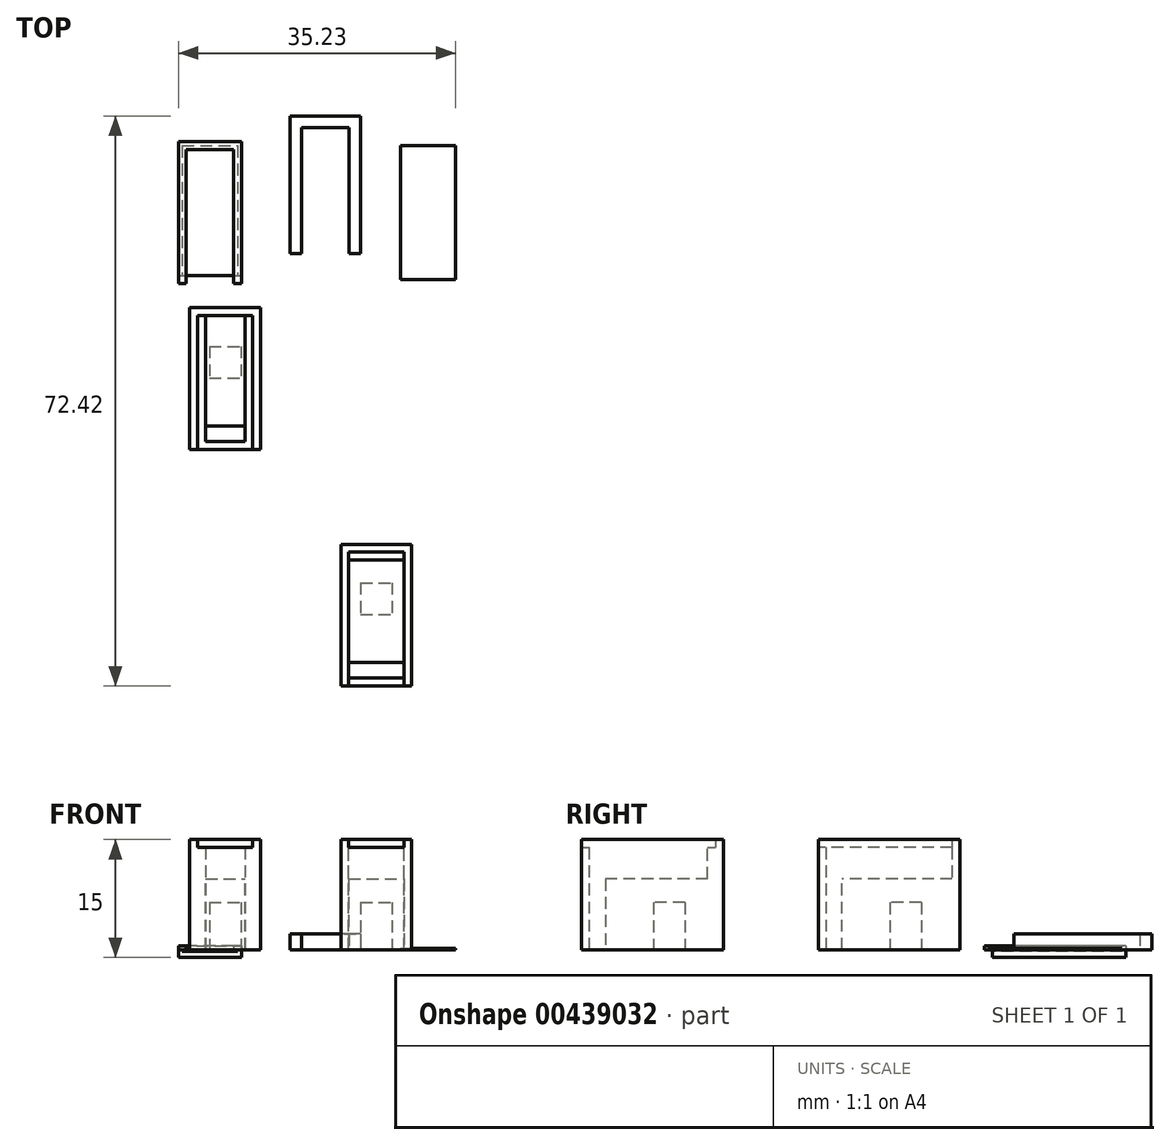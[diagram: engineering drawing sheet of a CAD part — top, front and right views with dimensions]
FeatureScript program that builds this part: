
annotation { "Feature Type Name" : "Feature", "Feature Type Description" : "" }
export const myFeature = defineFeature(function(context is Context, id is Id, definition is map)
    precondition{}
    {
        {
            var Q0;
            Q0=qCreatedBy(makeId("Top.planeOp"),FACE);
            var sketch = newSketch(context, id + "F0", { "sketchPlane" : qUnion([Q0])});
            skLineSegment(sketch, "E0.bottom", {"start": v(4.5, -9) * mm, "end": v(-4.5, -9) * mm});
            skLineSegment(sketch, "E0.top", {"start": v(4.5, 9) * mm, "end": v(-4.5, 9) * mm});
            skLineSegment(sketch, "E0.left", {"start": v(4.5, -9) * mm, "end": v(4.5, 9) * mm});
            skLineSegment(sketch, "E0.right", {"start": v(-4.5, -9) * mm, "end": v(-4.5, 9) * mm});
            skPoint(sketch, "E0.middle", {"position": v(0, 0) * mm});
            skSolve(sketch);
        }
        {
            var Q0;
            Q0=qSketchRegion(id+"F0",true);
            extrude(context, id + "F1", {"entities" : qUnion([Q0]), "depth" : 13 * mm});
        }
        {
            var Q0;
            Q0=makeQuery(id+"F1.opExtrude","CAP_FACE",FACE,{"disambiguationData":[OSD([sQuery(id+"F0.wireOp",EDGE,"E0.bottom"),sQuery(id+"F0.wireOp",EDGE,"E0.top"),sQuery(id+"F0.wireOp",EDGE,"E0.left"),sQuery(id+"F0.wireOp",EDGE,"E0.right")])],"isStart":true});
            var sketch = newSketch(context, id + "F2", { "sketchPlane" : qUnion([Q0])});
            skLineSegment(sketch, "E1.bottom", {"start": v(-2, -4.1) * mm, "end": v(2, -4.1) * mm});
            skLineSegment(sketch, "E1.top", {"start": v(-2, -0.1) * mm, "end": v(2, -0.1) * mm});
            skLineSegment(sketch, "E1.left", {"start": v(-2, -4.1) * mm, "end": v(-2, -0.1) * mm});
            skLineSegment(sketch, "E1.right", {"start": v(2, -4.1) * mm, "end": v(2, -0.1) * mm});
            skPoint(sketch, "E1.middle", {"position": v(0, -2.1) * mm});
            skSolve(sketch);
        }
        {
            var Q0;
            Q0=qSketchRegion(id+"F2",true);
            extrude(context, id + "F3", {"entities" : qUnion([Q0]), "operationType" : NewBodyOperationType.REMOVE, "oppositeDirection" : true, "depth" : 6 * mm});
        }
        {
            var Q0;
            Q0=makeQuery(id+"F1.opExtrude","SWEPT_FACE",FACE,{"disambiguationData":[OSD([sQuery(id+"F0.wireOp",EDGE,"E0.bottom")])]});
            var sketch = newSketch(context, id + "F4", { "sketchPlane" : qUnion([Q0])});
            skLineSegment(sketch, "E2.bottom", {"start": v(-2.5, 13) * mm, "end": v(2.5, 13) * mm});
            skLineSegment(sketch, "E2.top", {"start": v(-2.5, 9) * mm, "end": v(2.5, 9) * mm});
            skLineSegment(sketch, "E2.left", {"start": v(-2.5, 13) * mm, "end": v(-2.5, 9) * mm});
            skLineSegment(sketch, "E2.right", {"start": v(2.5, 13) * mm, "end": v(2.5, 9) * mm});
            skSolve(sketch);
        }
        {
            var Q0;
            Q0=qSketchRegion(id+"F4",true);
            extrude(context, id + "F5", {"entities" : qUnion([Q0]), "operationType" : NewBodyOperationType.REMOVE, "oppositeDirection" : true, "depth" : 17 * mm});
        }
        {
            var Q0;
            Q0=qCreatedBy(makeId("Top.planeOp"),FACE);
            var sketch = newSketch(context, id + "F6", { "sketchPlane" : qUnion([Q0])});
            skLineSegment(sketch, "E3", {"start": v(-5.95, 12.1) * mm, "end": v(-5.95, 30.1) * mm});
            skLineSegment(sketch, "E4", {"start": v(-5.95, 30.1) * mm, "end": v(2.05, 30.1) * mm});
            skLineSegment(sketch, "E5", {"start": v(2.05, 30.1) * mm, "end": v(2.05, 12.1) * mm});
            skLineSegment(sketch, "E6", {"start": v(2.05, 12.1) * mm, "end": v(1.05, 12.1) * mm});
            skLineSegment(sketch, "E7", {"start": v(1.05, 12.1) * mm, "end": v(1.05, 29.1) * mm});
            skLineSegment(sketch, "E8", {"start": v(1.05, 29.1) * mm, "end": v(-4.95, 29.1) * mm});
            skLineSegment(sketch, "E9", {"start": v(-4.95, 29.1) * mm, "end": v(-4.95, 12.1) * mm});
            skLineSegment(sketch, "E10", {"start": v(-4.95, 12.1) * mm, "end": v(-5.95, 12.1) * mm});
            skSolve(sketch);
        }
        {
            var Q0;
            Q0=qSketchRegion(id+"F6",true);
            extrude(context, id + "F7", {"entities" : qUnion([Q0]), "depth" : 0.5 * mm});
        }
        {
            var Q0;
            Q0=qCreatedBy(makeId("Top.planeOp"),FACE);
            var sketch = newSketch(context, id + "F8", { "sketchPlane" : qUnion([Q0])});
            skLineSegment(sketch, "E11.bottom", {"start": v(-5.95, 13.1) * mm, "end": v(2.05, 13.1) * mm});
            skLineSegment(sketch, "E11.top", {"start": v(-5.95, 30.1) * mm, "end": v(2.05, 30.1) * mm});
            skLineSegment(sketch, "E11.left", {"start": v(-5.95, 13.1) * mm, "end": v(-5.95, 30.1) * mm});
            skLineSegment(sketch, "E11.right", {"start": v(2.05, 13.1) * mm, "end": v(2.05, 30.1) * mm});
            skSolve(sketch);
        }
        {
            var Q0;
            Q0=qSketchRegion(id+"F8",true);
            extrude(context, id + "F9", {"entities" : qUnion([Q0]), "oppositeDirection" : true, "depth" : 1 * mm});
        }
        {
            var Q0;
            Q0=makeQuery(id+"F9.opExtrude","SWEPT_FACE",FACE,{"disambiguationData":[OSD([sQuery(id+"F8.wireOp",EDGE,"E11.bottom")])]});
            var sketch = newSketch(context, id + "F10", { "sketchPlane" : qUnion([Q0])});
            skLineSegment(sketch, "E12.bottom", {"start": v(-5.45, 0) * mm, "end": v(1.55, 0) * mm});
            skLineSegment(sketch, "E12.top", {"start": v(-5.45, -0.2) * mm, "end": v(1.55, -0.2) * mm});
            skLineSegment(sketch, "E12.left", {"start": v(-5.45, 0) * mm, "end": v(-5.45, -0.2) * mm});
            skLineSegment(sketch, "E12.right", {"start": v(1.55, 0) * mm, "end": v(1.55, -0.2) * mm});
            skSolve(sketch);
        }
        {
            var Q0;
            Q0=qSketchRegion(id+"F10",true);
            extrude(context, id + "F11", {"entities" : qUnion([Q0]), "operationType" : NewBodyOperationType.REMOVE, "oppositeDirection" : true, "depth" : 16.5 * mm});
        }
        {
            var Q0;
            Q0=qCreatedBy(makeId("Top.planeOp"),FACE);
            var sketch = newSketch(context, id + "F12", { "sketchPlane" : qUnion([Q0])});
            skLineSegment(sketch, "E13", {"start": v(8.22, 15.87) * mm, "end": v(8.22, 33.37) * mm});
            skLineSegment(sketch, "E14", {"start": v(8.22, 33.37) * mm, "end": v(17.22, 33.37) * mm});
            skLineSegment(sketch, "E15", {"start": v(17.22, 33.37) * mm, "end": v(17.22, 15.87) * mm});
            skLineSegment(sketch, "E16", {"start": v(17.22, 15.87) * mm, "end": v(15.72, 15.87) * mm});
            skLineSegment(sketch, "E17", {"start": v(15.72, 15.87) * mm, "end": v(15.72, 31.87) * mm});
            skLineSegment(sketch, "E18", {"start": v(15.72, 31.87) * mm, "end": v(9.72, 31.87) * mm});
            skLineSegment(sketch, "E19", {"start": v(9.72, 31.87) * mm, "end": v(9.72, 15.87) * mm});
            skLineSegment(sketch, "E20", {"start": v(9.72, 15.87) * mm, "end": v(8.22, 15.87) * mm});
            skSolve(sketch);
        }
        {
            var Q0;
            Q0=qSketchRegion(id+"F12",true);
            extrude(context, id + "F13", {"entities" : qUnion([Q0]), "depth" : 2 * mm});
        }
        {
            var Q0;
            Q0=qCreatedBy(makeId("Top.planeOp"),FACE);
            var sketch = newSketch(context, id + "F14", { "sketchPlane" : qUnion([Q0])});
            skLineSegment(sketch, "E21.bottom", {"start": v(22.28, 12.58) * mm, "end": v(29.28, 12.58) * mm});
            skLineSegment(sketch, "E21.top", {"start": v(22.28, 29.58) * mm, "end": v(29.28, 29.58) * mm});
            skLineSegment(sketch, "E21.left", {"start": v(22.28, 12.58) * mm, "end": v(22.28, 29.58) * mm});
            skLineSegment(sketch, "E21.right", {"start": v(29.28, 12.58) * mm, "end": v(29.28, 29.58) * mm});
            skSolve(sketch);
        }
        {
            var Q0;
            Q0=qSketchRegion(id+"F14",true);
            extrude(context, id + "F15", {"entities" : qUnion([Q0]), "depth" : 0.2 * mm});
        }
        {
            var Q0;
            Q0=makeQuery(id+"F5.boolean.opBoolean","COPY",FACE,{"derivedFrom":makeQuery(id+"F5.opExtrude","SWEPT_FACE",FACE,{"disambiguationData":[OSD([sQuery(id+"F4.wireOp",EDGE,"E2.top")])]})});
            var sketch = newSketch(context, id + "F16", { "sketchPlane" : qUnion([Q0])});
            skLineSegment(sketch, "E22.bottom", {"start": v(-2.5, -9) * mm, "end": v(2.5, -9) * mm});
            skLineSegment(sketch, "E22.top", {"start": v(-2.5, -6) * mm, "end": v(2.5, -6) * mm});
            skLineSegment(sketch, "E22.left", {"start": v(-2.5, -9) * mm, "end": v(-2.5, -6) * mm});
            skLineSegment(sketch, "E22.right", {"start": v(2.5, -9) * mm, "end": v(2.5, -6) * mm});
            skSolve(sketch);
        }
        {
            var Q0;
            Q0=qSketchRegion(id+"F16",true);
            extrude(context, id + "F17", {"entities" : qUnion([Q0]), "operationType" : NewBodyOperationType.REMOVE, "oppositeDirection" : true, "depth" : 25 * mm});
        }
        {
            var Q0;
            Q0=makeQuery(id+"F1.opExtrude","CAP_FACE",FACE,{"disambiguationData":[OSD([sQuery(id+"F0.wireOp",EDGE,"E0.bottom"),sQuery(id+"F0.wireOp",EDGE,"E0.top"),sQuery(id+"F0.wireOp",EDGE,"E0.left"),sQuery(id+"F0.wireOp",EDGE,"E0.right")])],"isStart":false});
            var sketch = newSketch(context, id + "F18", { "sketchPlane" : qUnion([Q0])});
            skLineSegment(sketch, "E23", {"start": v(-4.5, -9) * mm, "end": v(-4.5, 9) * mm});
            skLineSegment(sketch, "E24", {"start": v(-4.5, 9) * mm, "end": v(4.5, 9) * mm});
            skLineSegment(sketch, "E25", {"start": v(4.5, 9) * mm, "end": v(4.5, -9) * mm});
            skLineSegment(sketch, "E26", {"start": v(4.5, -9) * mm, "end": v(3.5, -9) * mm});
            skLineSegment(sketch, "E27", {"start": v(3.5, -9) * mm, "end": v(3.5, 8) * mm});
            skLineSegment(sketch, "E28", {"start": v(3.5, 8) * mm, "end": v(-3.5, 8) * mm});
            skLineSegment(sketch, "E29", {"start": v(-3.5, 8) * mm, "end": v(-3.5, -9) * mm});
            skLineSegment(sketch, "E30", {"start": v(-3.5, -9) * mm, "end": v(-4.5, -9) * mm});
            skSolve(sketch);
        }
        {
            var Q0;
            Q0=qSketchRegion(id+"F18",true);
            extrude(context, id + "F19", {"entities" : qUnion([Q0]), "operationType" : NewBodyOperationType.ADD, "depth" : 1 * mm});
        }
        {
            var Q0;
            Q0=makeQuery(id+"F1.opExtrude","CAP_FACE",FACE,{"disambiguationData":[OSD([sQuery(id+"F0.wireOp",EDGE,"E0.bottom"),sQuery(id+"F0.wireOp",EDGE,"E0.top"),sQuery(id+"F0.wireOp",EDGE,"E0.left"),sQuery(id+"F0.wireOp",EDGE,"E0.right")])],"isStart":true});
            var sketch = newSketch(context, id + "F20", { "sketchPlane" : qUnion([Q0])});
            skLineSegment(sketch, "E31.bottom", {"start": v(2.5, 9) * mm, "end": v(-2.5, 9) * mm});
            skLineSegment(sketch, "E31.top", {"start": v(2.5, 8) * mm, "end": v(-2.5, 8) * mm});
            skLineSegment(sketch, "E31.left", {"start": v(2.5, 9) * mm, "end": v(2.5, 8) * mm});
            skLineSegment(sketch, "E31.right", {"start": v(-2.5, 9) * mm, "end": v(-2.5, 8) * mm});
            skSolve(sketch);
        }
        {
            var Q0;
            Q0=qSketchRegion(id+"F20",true);
            extrude(context, id + "F21", {"entities" : qUnion([Q0]), "operationType" : NewBodyOperationType.ADD, "oppositeDirection" : true, "depth" : 13 * mm});
        }
        {
            var Q0;
            Q0=qCreatedBy(makeId("Top.planeOp"),FACE);
            var sketch = newSketch(context, id + "F22", { "sketchPlane" : qUnion([Q0])});
            skLineSegment(sketch, "E32.bottom", {"start": v(23.68, -21.05) * mm, "end": v(14.68, -21.05) * mm});
            skLineSegment(sketch, "E32.top", {"start": v(23.68, -39.05) * mm, "end": v(14.68, -39.05) * mm});
            skLineSegment(sketch, "E32.left", {"start": v(23.68, -21.05) * mm, "end": v(23.68, -39.05) * mm});
            skLineSegment(sketch, "E32.right", {"start": v(14.68, -21.05) * mm, "end": v(14.68, -39.05) * mm});
            skPoint(sketch, "E32.middle", {"position": v(19.18, -30.05) * mm});
            skSolve(sketch);
        }
        {
            var Q0;
            Q0=qSketchRegion(id+"F22",true);
            extrude(context, id + "F23", {"entities" : qUnion([Q0]), "depth" : 13 * mm});
        }
        {
            var Q0;
            Q0=makeQuery(id+"F23.opExtrude","CAP_FACE",FACE,{"disambiguationData":[OSD([sQuery(id+"F22.wireOp",EDGE,"E32.bottom"),sQuery(id+"F22.wireOp",EDGE,"E32.top"),sQuery(id+"F22.wireOp",EDGE,"E32.left"),sQuery(id+"F22.wireOp",EDGE,"E32.right")])],"isStart":false});
            var sketch = newSketch(context, id + "F24", { "sketchPlane" : qUnion([Q0])});
            skLineSegment(sketch, "E33.bottom", {"start": v(15.68, -23.05) * mm, "end": v(22.68, -23.05) * mm});
            skLineSegment(sketch, "E33.top", {"start": v(15.68, -38.05) * mm, "end": v(22.68, -38.05) * mm});
            skLineSegment(sketch, "E33.left", {"start": v(15.68, -23.05) * mm, "end": v(15.68, -38.05) * mm});
            skLineSegment(sketch, "E33.right", {"start": v(22.68, -23.05) * mm, "end": v(22.68, -38.05) * mm});
            skSolve(sketch);
        }
        {
            var Q0;
            Q0=qSketchRegion(id+"F24",true);
            extrude(context, id + "F25", {"entities" : qUnion([Q0]), "operationType" : NewBodyOperationType.REMOVE, "oppositeDirection" : true, "depth" : 4 * mm});
        }
        {
            var Q0;
            Q0=makeQuery(id+"F23.opExtrude","CAP_FACE",FACE,{"disambiguationData":[OSD([sQuery(id+"F22.wireOp",EDGE,"E32.bottom"),sQuery(id+"F22.wireOp",EDGE,"E32.top"),sQuery(id+"F22.wireOp",EDGE,"E32.left"),sQuery(id+"F22.wireOp",EDGE,"E32.right")])],"isStart":true});
            var sketch = newSketch(context, id + "F26", { "sketchPlane" : qUnion([Q0])});
            skLineSegment(sketch, "E34.bottom", {"start": v(17.18, 25.95) * mm, "end": v(21.18, 25.95) * mm});
            skLineSegment(sketch, "E34.top", {"start": v(17.18, 29.95) * mm, "end": v(21.18, 29.95) * mm});
            skLineSegment(sketch, "E34.left", {"start": v(17.18, 25.95) * mm, "end": v(17.18, 29.95) * mm});
            skLineSegment(sketch, "E34.right", {"start": v(21.18, 25.95) * mm, "end": v(21.18, 29.95) * mm});
            skPoint(sketch, "E34.middle", {"position": v(19.18, 27.95) * mm});
            skLineSegment(sketch, "E35.bottom", {"start": v(22.68, 36.05) * mm, "end": v(15.68, 36.05) * mm});
            skLineSegment(sketch, "E35.top", {"start": v(22.68, 38.05) * mm, "end": v(15.68, 38.05) * mm});
            skLineSegment(sketch, "E35.left", {"start": v(22.68, 36.05) * mm, "end": v(22.68, 38.05) * mm});
            skLineSegment(sketch, "E35.right", {"start": v(15.68, 36.05) * mm, "end": v(15.68, 38.05) * mm});
            skPoint(sketch, "E35.middle", {"position": v(19.18, 37.05) * mm});
            skSolve(sketch);
        }
        {
            var Q0;
            Q0=makeQuery(id+"F26.imprint","IMPRINT",FACE,{"disambiguationData":[TD([[makeQuery(id+"F26.imprint","IMPRINT",EDGE,{"derivedFrom":sQuery(id+"F26.wireOp",EDGE,"E34.bottom")}),1.0]])]});
            extrude(context, id + "F27", {"entities" : qUnion([Q0]), "operationType" : NewBodyOperationType.REMOVE, "oppositeDirection" : true, "depth" : 6 * mm});
        }
        {
            var Q0;
            Q0=makeQuery(id+"F26.imprint","IMPRINT",FACE,{"disambiguationData":[TD([[makeQuery(id+"F26.imprint","IMPRINT",EDGE,{"derivedFrom":sQuery(id+"F26.wireOp",EDGE,"E35.bottom")}),-1.0]])]});
            extrude(context, id + "F28", {"entities" : qUnion([Q0]), "operationType" : NewBodyOperationType.REMOVE, "oppositeDirection" : true, "depth" : 9 * mm});
        }
        {
            var Q0;
            Q0=makeQuery(id+"F23.opExtrude","CAP_FACE",FACE,{"disambiguationData":[OSD([sQuery(id+"F22.wireOp",EDGE,"E32.bottom"),sQuery(id+"F22.wireOp",EDGE,"E32.top"),sQuery(id+"F22.wireOp",EDGE,"E32.left"),sQuery(id+"F22.wireOp",EDGE,"E32.right")])],"isStart":false});
            var sketch = newSketch(context, id + "F29", { "sketchPlane" : qUnion([Q0])});
            skLineSegment(sketch, "E36", {"start": v(14.68, -39.05) * mm, "end": v(14.68, -21.05) * mm});
            skLineSegment(sketch, "E37", {"start": v(14.68, -21.05) * mm, "end": v(23.68, -21.05) * mm});
            skLineSegment(sketch, "E38", {"start": v(23.68, -21.05) * mm, "end": v(23.68, -39.05) * mm});
            skLineSegment(sketch, "E39", {"start": v(23.68, -39.05) * mm, "end": v(22.68, -39.05) * mm});
            skLineSegment(sketch, "E40", {"start": v(22.68, -39.05) * mm, "end": v(22.68, -22.05) * mm});
            skLineSegment(sketch, "E41", {"start": v(22.68, -22.05) * mm, "end": v(15.68, -22.05) * mm});
            skLineSegment(sketch, "E42", {"start": v(15.68, -22.05) * mm, "end": v(15.68, -39.05) * mm});
            skLineSegment(sketch, "E43", {"start": v(15.68, -39.05) * mm, "end": v(14.68, -39.05) * mm});
            skSolve(sketch);
        }
        {
            var Q0;
            Q0=qSketchRegion(id+"F29",true);
            extrude(context, id + "F30", {"entities" : qUnion([Q0]), "operationType" : NewBodyOperationType.ADD, "depth" : 1 * mm});
        }
    });
